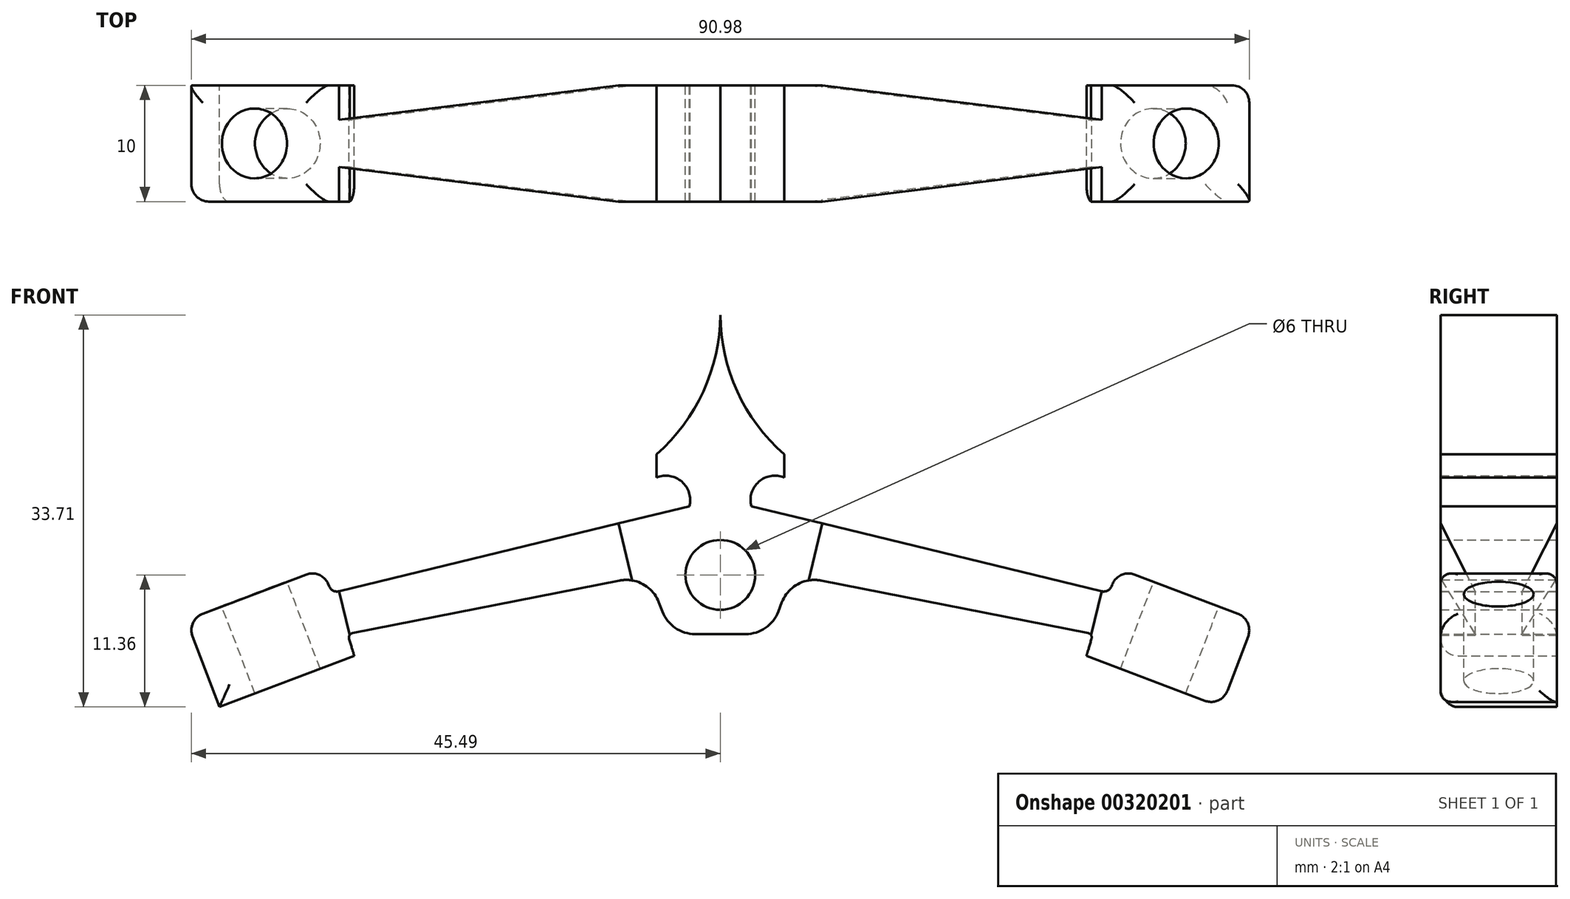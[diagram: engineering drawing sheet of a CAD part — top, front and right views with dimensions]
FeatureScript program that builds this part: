
annotation { "Feature Type Name" : "Feature", "Feature Type Description" : "" }
export const myFeature = defineFeature(function(context is Context, id is Id, definition is map)
    precondition{}
    {
        {
            var Q0;
            Q0=qCreatedBy(makeId("Front.planeOp"),FACE);
            var sketch = newSketch(context, id + "F0", { "sketchPlane" : qUnion([Q0])});
            skCircle(sketch, "E0", {"center": v(0, 0) * mm, "radius": 3 * mm});
            skLineSegment(sketch, "E1", {"start": v(0, 27.33) * mm, "end": v(0, -25.95) * mm, "construction": true});
            skLineSegment(sketch, "E2", {"start": v(0, 0) * mm, "end": v(-38.44, -14.62) * mm, "construction": true});
            skLineSegment(sketch, "E3", {"start": v(-31.5, -6.95) * mm, "end": v(-43.08, -11.36) * mm});
            skLineSegment(sketch, "E4", {"start": v(-43.08, -11.36) * mm, "end": v(-45.93, -3.88) * mm});
            skLineSegment(sketch, "E5", {"start": v(-45.93, -3.88) * mm, "end": v(-34.2, 0.57) * mm});
            skPoint(sketch, "E6.orphan", {"position": v(0, 22.6) * mm});
            skLineSegment(sketch, "E7", {"start": v(0, -5.09) * mm, "end": v(-2.18, -5.09) * mm});
            skLineSegment(sketch, "E8", {"start": v(-4.99, -3.16) * mm, "end": v(-5.29, -2.37) * mm});
            skLineSegment(sketch, "E9", {"start": v(-8.67, -0.49) * mm, "end": v(-31.63, -5) * mm});
            skLineSegment(sketch, "E10", {"start": v(-32.8, -1.41) * mm, "end": v(-2.66, 5.9) * mm});
            skArc(sketch, "E11", {"start": v(-5.48, 10.37) * mm, "mid": v(-1.4, 15.88) * mm, "end": v(0, 22.6) * mm});
            skLineSegment(sketch, "E12", {"start": v(-5.48, 10.37) * mm, "end": v(-5.48, 8.37) * mm});
            skArc(sketch, "E13", {"start": v(-2.66, 5.9) * mm, "mid": v(-3.3, 8) * mm, "end": v(-5.48, 8.37) * mm});
            skPoint(sketch, "E14.visualSharp", {"position": v(-6.19, 0) * mm});
            skArc(sketch, "E14.filletArc", {"start": v(-5.29, -2.37) * mm, "mid": v(-6.64, -0.8) * mm, "end": v(-8.67, -0.49) * mm});
            skPoint(sketch, "E15.visualSharp", {"position": v(-4.25, -5.09) * mm});
            skArc(sketch, "E15.filletArc", {"start": v(-4.99, -3.16) * mm, "mid": v(-3.88, -4.56) * mm, "end": v(-2.18, -5.09) * mm});
            skPoint(sketch, "E16.newPointA", {"position": v(-32.05, -5.09) * mm});
            skLineSegment(sketch, "E17", {"start": v(-34.2, 0.57) * mm, "end": v(-33.66, -0.95) * mm});
            skPoint(sketch, "E18.newPointB", {"position": v(-31.5, -6.95) * mm});
            skArc(sketch, "E18.filletArc", {"start": v(-33.66, -0.95) * mm, "mid": v(-33.32, -1.34) * mm, "end": v(-32.8, -1.41) * mm});
            skLineSegment(sketch, "E19", {"start": v(-31.93, -5.5) * mm, "end": v(-31.5, -6.95) * mm});
            skArc(sketch, "E20.filletArc", {"start": v(-31.63, -5) * mm, "mid": v(-31.89, -5.19) * mm, "end": v(-31.93, -5.5) * mm});
            skLineSegment(sketch, "E21", {"start": v(-40.07, -1.66) * mm, "end": v(-37.22, -9.13) * mm, "construction": true});
            skArc(sketch, "E22.MirrorCS", {"start": v(5.48, 10.37) * mm, "mid": v(1.4, 15.88) * mm, "end": v(0, 22.6) * mm});
            skLineSegment(sketch, "E23.MirrorCS", {"start": v(5.48, 10.37) * mm, "end": v(5.48, 8.37) * mm});
            skArc(sketch, "E24.MirrorCS", {"start": v(2.66, 5.9) * mm, "mid": v(3.3, 8) * mm, "end": v(5.48, 8.37) * mm});
            skLineSegment(sketch, "E25.MirrorCS", {"start": v(32.8, -1.41) * mm, "end": v(2.66, 5.9) * mm});
            skArc(sketch, "E26.MirrorCS", {"start": v(33.66, -0.95) * mm, "mid": v(33.32, -1.34) * mm, "end": v(32.8, -1.41) * mm});
            skLineSegment(sketch, "E27.MirrorCS", {"start": v(34.2, 0.57) * mm, "end": v(33.66, -0.95) * mm});
            skLineSegment(sketch, "E28.MirrorCS", {"start": v(45.93, -3.88) * mm, "end": v(34.2, 0.57) * mm});
            skLineSegment(sketch, "E29.MirrorCS", {"start": v(40.07, -1.66) * mm, "end": v(37.22, -9.13) * mm, "construction": true});
            skLineSegment(sketch, "E30.MirrorCS", {"start": v(43.08, -11.36) * mm, "end": v(45.93, -3.88) * mm});
            skLineSegment(sketch, "E31.MirrorCS", {"start": v(31.5, -6.95) * mm, "end": v(43.08, -11.36) * mm});
            skLineSegment(sketch, "E32.MirrorCS", {"start": v(31.93, -5.5) * mm, "end": v(31.5, -6.95) * mm});
            skArc(sketch, "E33.MirrorCS", {"start": v(31.63, -5) * mm, "mid": v(31.89, -5.19) * mm, "end": v(31.93, -5.5) * mm});
            skLineSegment(sketch, "E34.MirrorCS", {"start": v(8.67, -0.49) * mm, "end": v(31.63, -5) * mm});
            skArc(sketch, "E35.MirrorCS", {"start": v(5.29, -2.37) * mm, "mid": v(6.64, -0.8) * mm, "end": v(8.67, -0.49) * mm});
            skLineSegment(sketch, "E36.MirrorCS", {"start": v(4.99, -3.16) * mm, "end": v(5.29, -2.37) * mm});
            skArc(sketch, "E37.MirrorCS", {"start": v(4.99, -3.16) * mm, "mid": v(3.88, -4.56) * mm, "end": v(2.18, -5.09) * mm});
            skLineSegment(sketch, "E38.MirrorCS", {"start": v(0, -5.09) * mm, "end": v(2.18, -5.09) * mm});
            skSolve(sketch);
        }
        {
            var Q0;
            Q0 = qSketchRegion(id + "F0", true);
            extrude(context, id + "F1", {"entities" : qUnion([Q0]), "endBound" : BoundingType.SYMMETRIC, "depth" : 10 * mm});
        }
        {
            var Q0;
            Q0=makeQuery(id+"F1.opExtrude","SWEPT_FACE",FACE,{"disambiguationData":[OSD([sQuery(id+"F0.wireOp",EDGE,"E10")])]});
            var sketch = newSketch(context, id + "F2", { "sketchPlane" : qUnion([Q0])});
            skLineSegment(sketch, "E39", {"start": v(-7.48, 5) * mm, "end": v(-32.21, 2.02) * mm});
            skLineSegment(sketch, "E40.MirrorCS", {"start": v(-7.48, -5) * mm, "end": v(-32.21, -2.02) * mm});
            skPoint(sketch, "E41.orphan", {"position": v(35.3, 2.02) * mm});
            skPoint(sketch, "E42.orphan", {"position": v(35.3, -2.02) * mm});
            skSolve(sketch);
        }
        {
            var Q0;
            {var subQ0=sQuery(id+"F2.wireOp",EDGE,"E40.MirrorCS");Q0=makeQuery(id+"F2.imprint","IMPRINT",FACE,{"disambiguationData":[TD([[makeQuery(id+"F2.imprint","IMPRINT",EDGE,{"derivedFrom":subQ0}),1.0]])]});}
            var Q1;
            {var subQ0=sQuery(id+"F2.wireOp",EDGE,"E39");Q1=makeQuery(id+"F2.imprint","IMPRINT",FACE,{"disambiguationData":[TD([[makeQuery(id+"F2.imprint","IMPRINT",EDGE,{"derivedFrom":subQ0}),-1.0]])]});}
            extrude(context, id + "F3", {"entities" : qUnion([Q0, Q1]), "operationType" : NewBodyOperationType.REMOVE, "oppositeDirection" : true, "depth" : 25 * mm});
        }
        {
            var Q0;
            Q0=makeQuery(id+"F1.opExtrude","SWEPT_FACE",FACE,{"disambiguationData":[OSD([sQuery(id+"F0.wireOp",EDGE,"E25.MirrorCS")])]});
            var sketch = newSketch(context, id + "F4", { "sketchPlane" : qUnion([Q0])});
            skLineSegment(sketch, "E43", {"start": v(32.21, 5) * mm, "end": v(32.21, 2.02) * mm, "construction": true});
            skLineSegment(sketch, "E44", {"start": v(32.21, 2.02) * mm, "end": v(7.48, 5) * mm});
            skLineSegment(sketch, "E45.MirrorCS", {"start": v(32.21, -2.02) * mm, "end": v(7.48, -5) * mm});
            skSolve(sketch);
        }
        {
            var Q0;
            Q0 = qSketchRegion(id + "F4", true);
            var Q1;
            {var subQ0=sQuery(id+"F4.wireOp",EDGE,"E44");Q1=makeQuery(id+"F4.imprint","IMPRINT",FACE,{"disambiguationData":[TD([[makeQuery(id+"F4.imprint","IMPRINT",EDGE,{"derivedFrom":subQ0}),-1.0]])]});}
            var Q2;
            {var subQ0=sQuery(id+"F4.wireOp",EDGE,"E45.MirrorCS");Q2=makeQuery(id+"F4.imprint","IMPRINT",FACE,{"disambiguationData":[TD([[makeQuery(id+"F4.imprint","IMPRINT",EDGE,{"derivedFrom":subQ0}),1.0]])]});}
            extrude(context, id + "F5", {"entities" : qUnion([Q0, Q1, Q2]), "operationType" : NewBodyOperationType.REMOVE, "oppositeDirection" : true, "depth" : 25 * mm});
        }
        {
            var Q0;
            Q0=makeQuery(id+"F1.opExtrude","SWEPT_FACE",FACE,{"disambiguationData":[OSD([sQuery(id+"F0.wireOp",EDGE,"E28.MirrorCS")])]});
            var sketch = newSketch(context, id + "F6", { "sketchPlane" : qUnion([Q0])});
            skCircle(sketch, "E46", {"center": v(38.04, 0) * mm, "radius": 3 * mm});
            skPoint(sketch, "E46.centerSnap0", {"position": v(38.04, -5) * mm});
            skSolve(sketch);
        }
        {
            var Q0;
            Q0 = qSketchRegion(id + "F6", true);
            extrude(context, id + "F7", {"entities" : qUnion([Q0]), "operationType" : NewBodyOperationType.REMOVE, "oppositeDirection" : true, "depth" : 25 * mm});
        }
        {
            var Q0;
            Q0=makeQuery(id+"F1.opExtrude","SWEPT_FACE",FACE,{"disambiguationData":[OSD([sQuery(id+"F0.wireOp",EDGE,"E5")])]});
            var sketch = newSketch(context, id + "F8", { "sketchPlane" : qUnion([Q0])});
            skCircle(sketch, "E47", {"center": v(-38.04, 0) * mm, "radius": 3 * mm});
            skPoint(sketch, "E47.centerSnap0", {"position": v(-38.04, -5) * mm});
            skPoint(sketch, "E47.centerSnap1", {"position": v(-44.3, 0) * mm});
            skSolve(sketch);
        }
        {
            var Q0;
            Q0 = qSketchRegion(id + "F8", true);
            extrude(context, id + "F9", {"entities" : qUnion([Q0]), "operationType" : NewBodyOperationType.REMOVE, "oppositeDirection" : true, "depth" : 25 * mm});
        }
        {
            var Q0;
            Q0=makeQuery(id+"F1.opExtrude","CAP_EDGE",EDGE,{"disambiguationData":[OSD([sQuery(id+"F0.wireOp",EDGE,"E5")])],"isStart":false});
            var Q1;
            Q1=makeQuery(id+"F1.opExtrude","SWEPT_EDGE",EDGE,{"disambiguationData":[OSD([sQuery(id+"F0.wireOp",EDGE,"E4"),sQuery(id+"F0.wireOp",EDGE,"E5")])]});
            var Q2;
            Q2=makeQuery(id+"F1.opExtrude","CAP_EDGE",EDGE,{"disambiguationData":[OSD([sQuery(id+"F0.wireOp",EDGE,"E5")])],"isStart":true});
            var Q3;
            Q3=makeQuery(id+"F1.opExtrude","SWEPT_EDGE",EDGE,{"disambiguationData":[OSD([sQuery(id+"F0.wireOp",EDGE,"E5"),sQuery(id+"F0.wireOp",EDGE,"E17")])]});
            var Q4;
            Q4=makeQuery(id+"F1.opExtrude","CAP_EDGE",EDGE,{"disambiguationData":[OSD([sQuery(id+"F0.wireOp",EDGE,"E3")])],"isStart":false});
            var Q5;
            Q5=makeQuery(id+"F1.opExtrude","CAP_EDGE",EDGE,{"disambiguationData":[OSD([sQuery(id+"F0.wireOp",EDGE,"E4")])],"isStart":false});
            var Q6;
            Q6=makeQuery(id+"F1.opExtrude","CAP_EDGE",EDGE,{"disambiguationData":[OSD([sQuery(id+"F0.wireOp",EDGE,"E28.MirrorCS")])],"isStart":false});
            var Q7;
            Q7=makeQuery(id+"F1.opExtrude","CAP_EDGE",EDGE,{"disambiguationData":[OSD([sQuery(id+"F0.wireOp",EDGE,"E28.MirrorCS")])],"isStart":true});
            var Q8;
            Q8=makeQuery(id+"F1.opExtrude","SWEPT_EDGE",EDGE,{"disambiguationData":[OSD([sQuery(id+"F0.wireOp",EDGE,"E28.MirrorCS"),sQuery(id+"F0.wireOp",EDGE,"E30.MirrorCS")])]});
            var Q9;
            Q9=makeQuery(id+"F1.opExtrude","SWEPT_EDGE",EDGE,{"disambiguationData":[OSD([sQuery(id+"F0.wireOp",EDGE,"E27.MirrorCS"),sQuery(id+"F0.wireOp",EDGE,"E28.MirrorCS")])]});
            var Q10;
            Q10=makeQuery(id+"F1.opExtrude","CAP_EDGE",EDGE,{"disambiguationData":[OSD([sQuery(id+"F0.wireOp",EDGE,"E31.MirrorCS")])],"isStart":false});
            var Q11;
            Q11=makeQuery(id+"F1.opExtrude","SWEPT_EDGE",EDGE,{"disambiguationData":[OSD([sQuery(id+"F0.wireOp",EDGE,"E30.MirrorCS"),sQuery(id+"F0.wireOp",EDGE,"E31.MirrorCS")])]});
            var Q12;
            Q12=makeQuery(id+"F1.opExtrude","CAP_EDGE",EDGE,{"disambiguationData":[OSD([sQuery(id+"F0.wireOp",EDGE,"E30.MirrorCS")])],"isStart":true});
            fillet(context, id + "F10", {"entities" : qUnion([Q0, Q1, Q2, Q3, Q4, Q5, Q6, Q7, Q8, Q9, Q10, Q11, Q12]), "radius" : 1.5 * mm, "tangentPropagation" : true, "allowEdgeOverflow" : false});
        }
        {
            var Q0;
            Q0=makeQuery(id+"F1.opExtrude","SWEPT_BODY",BODY,{"disambiguationData":[OSD([sQuery(id+"F0.wireOp",EDGE,"E11"),sQuery(id+"F0.wireOp",EDGE,"E22.MirrorCS")])]});
            deleteBodies(context, id + "F11", {"entities" : qUnion([Q0])});
        }
    });
